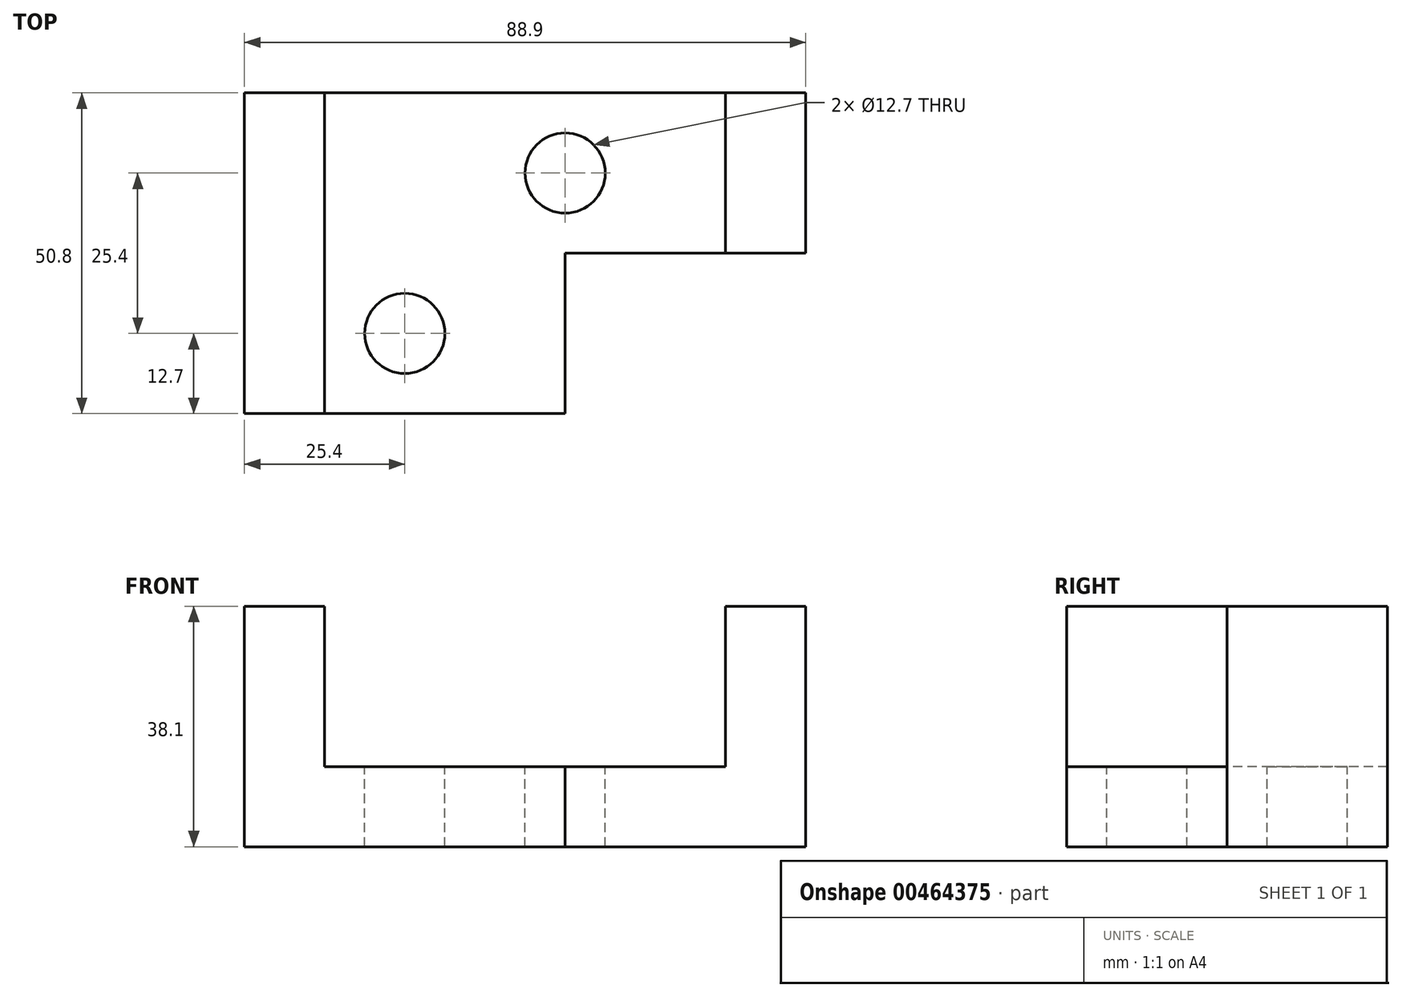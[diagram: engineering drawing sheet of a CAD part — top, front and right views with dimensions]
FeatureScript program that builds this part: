
annotation { "Feature Type Name" : "Feature", "Feature Type Description" : "" }
export const myFeature = defineFeature(function(context is Context, id is Id, definition is map)
    precondition{}
    {
        {
            var Q0;
            Q0=qCreatedBy(makeId("Front.planeOp"),FACE);
            var sketch = newSketch(context, id + "F0", { "sketchPlane" : qUnion([Q0])});
            skLineSegment(sketch, "E0.bottom", {"start": v(44.45, 19.05) * mm, "end": v(-44.45, 19.05) * mm});
            skLineSegment(sketch, "E0.top", {"start": v(44.45, -19.05) * mm, "end": v(-44.45, -19.05) * mm});
            skLineSegment(sketch, "E0.left", {"start": v(44.45, 19.05) * mm, "end": v(44.45, -19.05) * mm});
            skLineSegment(sketch, "E0.right", {"start": v(-44.45, 19.05) * mm, "end": v(-44.45, -19.05) * mm});
            skPoint(sketch, "E0.middle", {"position": v(0, 0) * mm});
            skSolve(sketch);
        }
        {
            var Q0;
            Q0 = qSketchRegion(id + "F0", true);
            extrude(context, id + "F1", {"entities" : qUnion([Q0]), "depth" : 50.8 * mm});
        }
        {
            var Q0;
            Q0=makeQuery(id+"F1.opExtrude","CAP_FACE",FACE,{"disambiguationData":[OSD([sQuery(id+"F0.wireOp",EDGE,"E0.bottom"),sQuery(id+"F0.wireOp",EDGE,"E0.top"),sQuery(id+"F0.wireOp",EDGE,"E0.left"),sQuery(id+"F0.wireOp",EDGE,"E0.right")])],"isStart":false});
            var sketch = newSketch(context, id + "F2", { "sketchPlane" : qUnion([Q0])});
            skLineSegment(sketch, "E1", {"start": v(-44.45, 19.05) * mm, "end": v(-31.75, 19.05) * mm});
            skLineSegment(sketch, "E2", {"start": v(-31.75, -6.35) * mm, "end": v(-31.75, 19.05) * mm});
            skLineSegment(sketch, "E3", {"start": v(-31.75, -6.35) * mm, "end": v(31.75, -6.35) * mm});
            skLineSegment(sketch, "E4", {"start": v(31.75, -6.35) * mm, "end": v(31.75, 19.05) * mm});
            skLineSegment(sketch, "E5", {"start": v(31.75, 19.05) * mm, "end": v(44.45, 19.05) * mm});
            skSolve(sketch);
        }
        {
            var Q0;
            {var subQ0=sQuery(id+"F2.wireOp",EDGE,"E2");Q0=makeQuery(id+"F2.imprint","IMPRINT",FACE,{"disambiguationData":[TD([[makeQuery(id+"F2.imprint","IMPRINT",EDGE,{"derivedFrom":subQ0}),-1.0]])]});}
            extrude(context, id + "F3", {"entities" : qUnion([Q0]), "operationType" : NewBodyOperationType.REMOVE, "endBound" : BoundingType.THROUGH_ALL, "oppositeDirection" : true, "depth" : 25.4 * mm});
        }
        {
            var Q0;
            Q0=makeQuery(id+"F3.boolean.opBoolean","COPY",FACE,{"derivedFrom":makeQuery(id+"F3.opExtrude","SWEPT_FACE",FACE,{"disambiguationData":[OSD([sQuery(id+"F2.wireOp",EDGE,"E3")])]})});
            var sketch = newSketch(context, id + "F4", { "sketchPlane" : qUnion([Q0])});
            skPoint(sketch, "E6.startSnap0", {"position": v(6.35, -25.4) * mm});
            skLineSegment(sketch, "E7.bottom", {"start": v(6.35, -25.4) * mm, "end": v(31.75, -25.4) * mm});
            skLineSegment(sketch, "E7.top", {"start": v(6.35, -50.8) * mm, "end": v(31.75, -50.8) * mm});
            skLineSegment(sketch, "E7.left", {"start": v(6.35, -25.4) * mm, "end": v(6.35, -50.8) * mm});
            skLineSegment(sketch, "E7.right", {"start": v(31.75, -25.4) * mm, "end": v(31.75, -50.8) * mm});
            skSolve(sketch);
        }
        {
            var Q0;
            Q0=makeQuery(id+"F4.imprint","IMPRINT",FACE,{"disambiguationData":[TD([[makeQuery(id+"F4.imprint","IMPRINT",EDGE,{"derivedFrom":sQuery(id+"F4.wireOp",EDGE,"E7.bottom")}),-1.0]])]});
            extrude(context, id + "F5", {"entities" : qUnion([Q0]), "operationType" : NewBodyOperationType.REMOVE, "endBound" : BoundingType.THROUGH_ALL, "oppositeDirection" : true, "depth" : 25.4 * mm});
        }
        {
            var Q0;
            {var subQ1=sQuery(id+"F0.wireOp",EDGE,"E0.left");var subQ3=sQuery(id+"F0.wireOp",EDGE,"E0.bottom");Q0=makeQuery(id+"F3.boolean.opBoolean","SPLIT",FACE,{"disambiguationData":[TD([makeQuery(id+"F1.opExtrude","SWEPT_FACE",FACE,{"disambiguationData":[OSD([subQ1])]})])],"derivedFrom":makeQuery(id+"F1.opExtrude","SWEPT_FACE",FACE,{"disambiguationData":[OSD([subQ3])]})});}
            var sketch = newSketch(context, id + "F6", { "sketchPlane" : qUnion([Q0])});
            skLineSegment(sketch, "E8.bottom", {"start": v(31.75, -25.4) * mm, "end": v(44.45, -25.4) * mm});
            skLineSegment(sketch, "E8.top", {"start": v(31.75, -50.8) * mm, "end": v(44.45, -50.8) * mm});
            skLineSegment(sketch, "E8.left", {"start": v(31.75, -25.4) * mm, "end": v(31.75, -50.8) * mm});
            skLineSegment(sketch, "E8.right", {"start": v(44.45, -25.4) * mm, "end": v(44.45, -50.8) * mm});
            skSolve(sketch);
        }
        {
            var Q0;
            Q0=makeQuery(id+"F6.imprint","IMPRINT",FACE,{"disambiguationData":[TD([[makeQuery(id+"F6.imprint","IMPRINT",EDGE,{"derivedFrom":sQuery(id+"F6.wireOp",EDGE,"E8.bottom")}),-1.0]])]});
            extrude(context, id + "F7", {"entities" : qUnion([Q0]), "operationType" : NewBodyOperationType.REMOVE, "endBound" : BoundingType.THROUGH_ALL, "oppositeDirection" : true, "depth" : 25.4 * mm});
        }
        {
            var Q0;
            Q0=makeQuery(id+"F3.boolean.opBoolean","COPY",FACE,{"derivedFrom":makeQuery(id+"F3.opExtrude","SWEPT_FACE",FACE,{"disambiguationData":[OSD([sQuery(id+"F2.wireOp",EDGE,"E3")])]})});
            var sketch = newSketch(context, id + "F8", { "sketchPlane" : qUnion([Q0])});
            skCircle(sketch, "E9", {"center": v(6.35, -12.7) * mm, "radius": 6.35 * mm});
            skSolve(sketch);
        }
        {
            var Q0;
            Q0=makeQuery(id+"F8.imprint","IMPRINT",FACE,{"disambiguationData":[TD([[makeQuery(id+"F8.imprint","IMPRINT",EDGE,{"derivedFrom":sQuery(id+"F8.wireOp",EDGE,"E9")}),1.0]])]});
            extrude(context, id + "F9", {"entities" : qUnion([Q0]), "operationType" : NewBodyOperationType.REMOVE, "endBound" : BoundingType.THROUGH_ALL, "oppositeDirection" : true, "depth" : 25.4 * mm});
        }
        {
            var Q0;
            Q0=makeQuery(id+"F3.boolean.opBoolean","COPY",FACE,{"derivedFrom":makeQuery(id+"F3.opExtrude","SWEPT_FACE",FACE,{"disambiguationData":[OSD([sQuery(id+"F2.wireOp",EDGE,"E3")])]})});
            var sketch = newSketch(context, id + "F10", { "sketchPlane" : qUnion([Q0])});
            skLineSegment(sketch, "E10", {"start": v(6.35, -50.8) * mm, "end": v(-19.05, -50.8) * mm});
            skLineSegment(sketch, "E11", {"start": v(6.35, -25.4) * mm, "end": v(6.35, -38.1) * mm});
            skPoint(sketch, "E12", {"position": v(-19.05, -38.1) * mm});
            skCircle(sketch, "E13", {"center": v(-19.05, -38.1) * mm, "radius": 6.35 * mm});
            skSolve(sketch);
        }
        {
            var Q0;
            Q0=makeQuery(id+"F10.imprint","IMPRINT",FACE,{"disambiguationData":[TD([[makeQuery(id+"F10.imprint","IMPRINT",EDGE,{"derivedFrom":sQuery(id+"F10.wireOp",EDGE,"E13")}),1.0]])]});
            extrude(context, id + "F11", {"entities" : qUnion([Q0]), "operationType" : NewBodyOperationType.REMOVE, "endBound" : BoundingType.THROUGH_ALL, "oppositeDirection" : true, "depth" : 25.4 * mm});
        }
    });
